FCSTD DOCUMENT  (FreeCAD 1.0R39319 (Git))
Label: Assignment_11.1_Knuckle_Joint_Assembly
License: All rights reserved
LicenseURL: https://en.wikipedia.org/wiki/All_rights_reserved
objects: TechDraw::DrawViewBalloon×10, App::FeaturePython×8, TechDraw::DrawViewAnnotation×6, TechDraw::DrawProjGroupItem×6, App::Link×5, TechDraw::DrawViewDimension×5, TechDraw::DrawSVGTemplate×2, TechDraw::DrawProjGroup×2, TechDraw::DrawPage×2, Assembly::JointGroup×1, Assembly::BomObject×1, Assembly::BomGroup×1, Spreadsheet::Sheet×1, TechDraw::DrawViewSpreadsheet×1, Assembly::ViewGroup×1, Assembly::AssemblyObject×1
note: 9 computed .brp shape members not serialized (recipe doc carries the construction recipe); baked Part::Feature solids carry a one-line shape summary decoded from their .brp
EXTERNAL_REF file=knuckle pin.FCStd obj=Body
EXTERNAL_REF file=Doube_eye.FCStd obj=Body
EXTERNAL_REF file=Eye End.FCStd obj=Body
EXTERNAL_REF file=taper pin.FCStd obj=Body
EXTERNAL_REF file=Coller.FCStd obj=Body

FEATURE [App::Link] knuckle_pin  label="knuckle pin"
  LinkedObject = -> <external knuckle pin.FCStd>#Body
FEATURE [App::FeaturePython] GroundedJoint  # Assembly grounded joint (typed FeaturePython)
  ObjectToGround = -> knuckle_pin
FEATURE [App::Link] Double_eye
  LinkPlacement = pos=(0,0,14.98) rot=(0,0,-1;1.56968rad)
  LinkedObject = -> <external Doube_eye.FCStd>#Body
  Placement = pos=(0,0,14.98) rot=(0,0,-1;1.56968rad)
FEATURE [App::Link] Single_Eye  label="Single Eye"
  LinkPlacement = pos=(0,0,37.0605) rot=(0,0,1;1.57134rad)
  LinkedObject = -> <external Eye End.FCStd>#Body
  Placement = pos=(0,0,37.0605) rot=(0,0,1;1.57134rad)
FEATURE [App::Link] taper_pin  label="taper pin"
  LinkPlacement = pos=(0,-27,102.1) rot=(1,0,0;4.71239rad)
  LinkedObject = -> <external taper pin.FCStd>#Body
  Placement = pos=(0,-27,102.1) rot=(1,0,0;4.71239rad)
FEATURE [App::FeaturePython] Joint  label="Revolute"  # Assembly joint (typed FeaturePython)
  Activated = true
  AngleMax = 130
  AngleMin = -15
  Detach1 = false
  Detach2 = false
  Distance = 0
  Distance2 = 0
  EnableAngleMax = true
  EnableAngleMin = true
  EnableLengthMax = false
  EnableLengthMin = false
  JointType = 1 (Revolute)
  LengthMax = 0
  LengthMin = 0
  Placement2 = pos=(0,0,14.98) rot=(0,0,1;0rad)
  Reference1 = -> Assembly [Double_eye.Face28,Double_eye.Edge1]
  Reference2 = -> Assembly [knuckle_pin.Face4,knuckle_pin.Edge1]
FEATURE [App::FeaturePython] Joint003  label="Fixed001"  # Assembly joint (typed FeaturePython)
  Activated = true
  AngleMax = 0
  AngleMin = 0
  Detach1 = false
  Detach2 = false
  Distance = 0
  Distance2 = 0
  EnableAngleMax = false
  EnableAngleMin = false
  EnableLengthMax = false
  EnableLengthMin = false
  JointType = 0 (Fixed)
  LengthMax = 0
  LengthMin = 0
  Offset2 = pos=(0,0,-25) rot=(0,0,1;0rad)
  Placement1 = pos=(0,1.42e-14,52) rot=(0,0,1;0rad)
  Placement2 = pos=(0,25,102.1) rot=(1,0,0;1.5708rad)
  Reference1 = -> Assembly [taper_pin.Face1,taper_pin.Edge3]
  Reference2 = -> Assembly [knuckle_pin.Face6,knuckle_pin.Face6]
FEATURE [App::FeaturePython] Joint004  label="Revolute001"  # Assembly joint (typed FeaturePython)
  Activated = true
  AngleMax = -70
  AngleMin = -180
  Detach1 = false
  Detach2 = false
  Distance = 0
  Distance2 = 0
  EnableAngleMax = true
  EnableAngleMin = true
  EnableLengthMax = false
  EnableLengthMin = false
  JointType = 1 (Revolute)
  LengthMax = 0
  LengthMin = 0
  Offset2 = pos=(0,0,7.215) rot=(0,0,1;0rad)
  Placement1 = pos=(0,0,35.98) rot=(0,0,1;0rad)
  Placement2 = pos=(0,0,73.0405) rot=(0,0,1;0rad)
  Reference1 = -> Assembly [Single_Eye.Edge41,Single_Eye.Edge41]
  Reference2 = -> Assembly [knuckle_pin.Face4,knuckle_pin.Face4]
FEATURE [TechDraw::DrawSVGTemplate] Template
  Height = 210
  Orientation = 1
  Template = C:/Program Files/FreeCAD 1.0/data/Mod/TechDraw/Templates/A4_Landscape_TD.svg
  Width = 297
FEATURE [TechDraw::DrawViewAnnotation] Annotation
  Font = osifont
  LineSpace = 100
  LockPosition = false
  MaxWidth = -1
  Rotation = 0
  ScaleType = 0
  Text = Front View
  TextSize = 5
  TextStyle = 0
  X = 108.227
  Y = 143.292
FEATURE [TechDraw::DrawViewAnnotation] Annotation001
  Font = osifont
  LineSpace = 100
  LockPosition = false
  MaxWidth = -1
  Rotation = 0
  ScaleType = 0
  Text = Top View
  TextSize = 5
  TextStyle = 0
  X = 108.227
  Y = 84.9012
FEATURE [TechDraw::DrawViewAnnotation] Annotation002
  Font = osifont
  LineSpace = 100
  LockPosition = false
  MaxWidth = -1
  Rotation = 0
  ScaleType = 0
  Text = Isometric View
  TextSize = 5
  TextStyle = 0
  X = 50.4437
  Y = 16.9549
FEATURE [TechDraw::DrawViewAnnotation] Annotation003
  Font = osifont
  LineSpace = 100
  LockPosition = false
  MaxWidth = -1
  Rotation = 0
  ScaleType = 0
  Text = Side View
  TextSize = 5
  TextStyle = 0
  X = 204.227
  Y = 143.292
FEATURE [App::Link] Coller
  LinkPlacement = pos=(0,0,95.1) rot=(0,0,1;1.5708rad)
  LinkedObject = -> <external Coller.FCStd>#Body
  Placement = pos=(0,0,95.1) rot=(0,0,1;1.5708rad)
FEATURE [App::FeaturePython] Joint005  label="Fixed"  # Assembly joint (typed FeaturePython)
  Activated = true
  AngleMax = 0
  AngleMin = 0
  Detach1 = false
  Detach2 = false
  Distance = 0
  Distance2 = 0
  EnableAngleMax = false
  EnableAngleMin = false
  EnableLengthMax = false
  EnableLengthMin = false
  JointType = 0 (Fixed)
  LengthMax = 0
  LengthMin = 0
  Offset2 = pos=(0,0,0) rot=(0,0,1;1.5708rad)
  Placement1 = pos=(0,0,7) rot=(0,0,1;0rad)
  Placement2 = pos=(0,0,102.1) rot=(0,0,1;1.5708rad)
  Reference1 = -> Assembly [Coller.Face6,Coller.Edge7]
  Reference2 = -> Assembly [knuckle_pin.Face4,knuckle_pin.Edge5]
FEATURE [Assembly::JointGroup] Joints
  Group = -> [GroundedJoint,Joint,Joint003,Joint004,Joint005]
FEATURE [Assembly::BomObject] Bill_of_Materials
  cells = A1='Index; B1='Name; C1='Quantity; A2='1; B2='knuckle pin; C2=1; A3='2; B3='Double_eye; C3=1; A4='3; B4='Single Eye; C4=1; A5='4; B5='taper pin; C5=1; A6='5; B6='Coller; C6=1
  columnsNames = Index | Name | Quantity
  detailParts = true
  detailSubAssemblies = true
  onlyParts = false
FEATURE [Assembly::BomGroup] Bills_of_Materials
  Group = -> [Bill_of_Materials]
FEATURE [Spreadsheet::Sheet] Spreadsheet
  cells = A1='Index; B1='Name; C1='Quantity; A2='1; B2='knuckle pin; C2=1; A3='2; B3='Double_eye; C3=1; A4='3; B4='Single Eye; C4=1; A5='4; B5='taper pin; C5=1; A6='5; B6='Coller; C6=1
FEATURE [TechDraw::DrawViewSpreadsheet] Sheet
  CellEnd = C6
  CellStart = A1
  Font = osifont
  LineWidth = 1.35
  LockPosition = false
  Rotation = 0
  ScaleType = 2
  Source = -> Bill_of_Materials
  Symbol = <blob: 3907 chars omitted>
  TextSize = 14
  X = 236.512
  Y = 91.6442
FEATURE [TechDraw::DrawViewAnnotation] Annotation004
  Font = osifont
  LineSpace = 100
  LockPosition = false
  MaxWidth = -1
  Rotation = 0
  ScaleType = 0
  Text = Bill of Material 
  TextSize = 4
  TextStyle = 0
  X = 236.512
  Y = 63.0244
FEATURE [TechDraw::DrawSVGTemplate] Template001
  Height = 210
  Orientation = 1
  Template = C:/Program Files/FreeCAD 1.0/data/Mod/TechDraw/Templates/A4_Landscape_TD.svg
  Width = 297
FEATURE [App::FeaturePython] Move  # WARN: FeaturePython — macro-defined, semantics opaque (R4)
  MoveType = 1
  MovementTransform = pos=(0,-2e-05,166) rot=(0,0,1;0rad)
  References = -> Assembly [knuckle_pin.,Double_eye.,Single_Eye.,taper_pin.,Coller.]
FEATURE [App::FeaturePython] Move001  # WARN: FeaturePython — macro-defined, semantics opaque (R4)
  MoveType = 0
  MovementTransform = pos=(73.0001,-3e-05,4e-05) rot=(-1.00436,0,0;0rad)
  References = -> Assembly [taper_pin.]
FEATURE [App::FeaturePython] Exploded_View  # WARN: FeaturePython — macro-defined, semantics opaque (R4)
  Group = -> [Move,Move001]
FEATURE [Assembly::ViewGroup] Exploded_Views
  Group = -> [Exploded_View]
FEATURE [Assembly::AssemblyObject] Assembly
  Group = -> [Joints,knuckle_pin,GroundedJoint,Double_eye,Single_Eye,taper_pin,Joint,Joint003,Joint004,Coller,Exploded_Views,Joint005,Bills_of_Materials,Exploded_View,Bill_of_Materials,Move,Move001]
  Origin = -> Origin
  Type = Assembly
FEATURE [TechDraw::DrawProjGroupItem] View  label="Front"
  CoarseView = false
  Direction = (0,-1,0)
  Focus = 100
  HardHidden = false
  IsoCount = 0
  IsoHidden = false
  IsoVisible = false
  LockPosition = true
  Perspective = false
  Rotation = 0
  RotationVector = (1,0,0)
  Scale = 0.25
  ScaleType = 2
  ScrubCount = 1
  SeamHidden = false
  SeamVisible = false
  SmoothHidden = false
  SmoothVisible = true
  Source = -> [Assembly]
  Type = 0
  X = 0
  XDirection = (1,0,0)
  Y = 0
FEATURE [TechDraw::DrawProjGroupItem] ProjItem  label="Top"
  CoarseView = false
  Direction = (0,0,1)
  Focus = 100
  HardHidden = false
  IsoCount = 0
  IsoHidden = false
  IsoVisible = false
  LockPosition = true
  Perspective = false
  Rotation = 0
  RotationVector = (1,0,0)
  Scale = 0.25
  ScaleType = 2
  ScrubCount = 1
  SeamHidden = false
  SeamVisible = false
  SmoothHidden = false
  SmoothVisible = true
  Source = -> [Assembly]
  Type = 4
  X = 0
  XDirection = (1,0,0)
  Y = -68.4206
FEATURE [TechDraw::DrawProjGroupItem] ProjItem001  label="Left"
  CoarseView = false
  Direction = (-1,-1e-16,0)
  Focus = 100
  HardHidden = false
  IsoCount = 0
  IsoHidden = false
  IsoVisible = false
  LockPosition = true
  Perspective = false
  Rotation = 0
  RotationVector = (1,0,0)
  Scale = 0.25
  ScaleType = 2
  ScrubCount = 1
  SeamHidden = false
  SeamVisible = false
  SmoothHidden = false
  SmoothVisible = true
  Source = -> [Assembly]
  Type = 1
  X = 96.1426
  XDirection = (1e-16,-1,0)
  Y = 0
FEATURE [TechDraw::DrawProjGroupItem] ProjItem002  label="FrontTopRight"
  CoarseView = false
  Direction = (0.57735,-0.57735,0.57735)
  Focus = 100
  HardHidden = false
  IsoCount = 0
  IsoHidden = false
  IsoVisible = false
  LockPosition = true
  Perspective = false
  Rotation = 0
  RotationVector = (1,0,0)
  Scale = 0.25
  ScaleType = 2
  ScrubCount = 1
  SeamHidden = false
  SeamVisible = false
  SmoothHidden = false
  SmoothVisible = true
  Source = -> [Assembly]
  Type = 7
  X = -57.6411
  XDirection = (0.707107,0.707107,0)
  Y = -123.101
FEATURE [TechDraw::DrawProjGroup] ProjGroup
  Anchor = -> View
  AutoDistribute = true
  LockPosition = false
  ProjectionType = 0
  Rotation = 0
  Scale = 0.25
  ScaleType = 1
  Source = -> [Assembly]
  Views = -> [View,ProjItem,ProjItem001,ProjItem002]
  X = 108.227
  Y = 167.894
  spacingX = 15
  spacingY = 15
FEATURE [TechDraw::DrawViewDimension] Dimension001
  AngleOverride = false
  Arbitrary = false
  ArbitraryTolerances = false
  BoxCorners = (2) [(-7.5,-14.625,-1e-07),(7.5,14.625,1e-07)]
  EqualTolerance = true
  ExtensionAngle = 0
  FormatSpec = %.2w
  FormatSpecOverTolerance = %+.2w
  FormatSpecUnderTolerance = %+.2w
  Inverted = false
  LineAngle = 0
  LockPosition = false
  MeasureType = 1
  OverTolerance = 0
  References2D = -> [ProjItem001]
  Rotation = 0
  ScaleType = 0
  TheoreticalExact = false
  Type = 0
  UnderTolerance = 0
  X = 27.0573
  Y = 0
FEATURE [TechDraw::DrawViewDimension] Dimension
  AngleOverride = false
  Arbitrary = false
  ArbitraryTolerances = false
  BoxCorners = (2) [(-43.3781,-14.625,-1e-07),(43.3781,14.625,1e-07)]
  EqualTolerance = true
  ExtensionAngle = 0
  FormatSpec = %.2w
  FormatSpecOverTolerance = %+.2w
  FormatSpecUnderTolerance = %+.2w
  Inverted = false
  LineAngle = 0
  LockPosition = false
  MeasureType = 1
  OverTolerance = 0
  References2D = -> [View]
  Rotation = 0
  ScaleType = 0
  TheoreticalExact = false
  Type = 0
  UnderTolerance = 0
  X = -0.000147
  Y = 32.917
FEATURE [TechDraw::DrawViewBalloon] Balloon
  BubbleShape = 0
  EndType = 0
  EndTypeScale = 1
  KinkLength = 5
  LockPosition = false
  OriginX = 3.36178
  OriginY = -57.0902
  Rotation = 0
  ScaleType = 0
  ShapeScale = 0.8
  SourceView = -> View
  Text = 1
  TextWrapLen = -1
  X = 94.7676
  Y = -79.7421
FEATURE [TechDraw::DrawViewBalloon] Balloon001
  BubbleShape = 0
  EndType = 0
  EndTypeScale = 1
  KinkLength = 5
  LockPosition = false
  OriginX = 51.8363
  OriginY = 24.6512
  Rotation = 0
  ScaleType = 0
  ShapeScale = 0.8
  SourceView = -> View
  Text = 2
  TextWrapLen = -1
  X = 129.46
  Y = 53.5628
FEATURE [TechDraw::DrawViewBalloon] Balloon002
  BubbleShape = 0
  EndType = 0
  EndTypeScale = 0.9
  KinkLength = 5
  LockPosition = false
  OriginX = -126.379
  OriginY = 17.9415
  Rotation = 0
  ScaleType = 0
  ShapeScale = 0.8
  SourceView = -> ProjItem
  Text = 3
  TextWrapLen = -1
  X = -138.193
  Y = 87.6891
FEATURE [TechDraw::DrawViewBalloon] Balloon003
  BubbleShape = 0
  EndType = 0
  EndTypeScale = 1
  KinkLength = 5
  LockPosition = false
  OriginX = 26.6327
  OriginY = 48.4784
  Rotation = 0
  ScaleType = 0
  ShapeScale = 0.8
  SourceView = -> ProjItem001
  Text = 4
  TextWrapLen = -1
  X = 82.7868
  Y = 94.8136
FEATURE [TechDraw::DrawViewBalloon] Balloon004
  BubbleShape = 0
  EndType = 0
  EndTypeScale = 1
  KinkLength = 5
  LockPosition = false
  OriginX = -3.66518
  OriginY = 9.87877
  Rotation = 0
  ScaleType = 0
  ShapeScale = 0.8
  SourceView = -> Balloon003
  Text = 5
  TextWrapLen = -1
  X = -24.8614
  Y = -3.60584
FEATURE [TechDraw::DrawProjGroupItem] View001  label="Front001"
  CoarseView = false
  Direction = (0,-1,0)
  Focus = 100
  HardHidden = false
  IsoCount = 0
  IsoHidden = false
  IsoVisible = false
  LockPosition = true
  Perspective = false
  Rotation = 0
  RotationVector = (1,0,0)
  Scale = 0.5
  ScaleType = 2
  ScrubCount = 1
  SeamHidden = false
  SeamVisible = false
  SmoothHidden = false
  SmoothVisible = true
  Source = -> [Exploded_View]
  Type = 0
  X = 0
  XDirection = (1,0,0)
  Y = 0
FEATURE [TechDraw::DrawViewAnnotation] Annotation005
  Font = osifont
  LineSpace = 100
  LockPosition = false
  MaxWidth = -1
  Rotation = 0
  ScaleType = 0
  Text = Exploded View
  TextSize = 5
  TextStyle = 0
  X = 143.116
  Y = 68.226
FEATURE [TechDraw::DrawProjGroupItem] ProjItem003  label="FrontTopLeft"
  CoarseView = false
  Direction = (-0.57735,-0.57735,0.57735)
  Focus = 100
  HardHidden = false
  IsoCount = 0
  IsoHidden = false
  IsoVisible = false
  LockPosition = true
  Perspective = false
  Rotation = 0
  RotationVector = (1,0,0)
  Scale = 0.5
  ScaleType = 2
  ScrubCount = 1
  SeamHidden = false
  SeamVisible = false
  SmoothHidden = false
  SmoothVisible = true
  Source = -> [Exploded_View]
  Type = 6
  X = -5.38404
  XDirection = (0.707107,-0.707107,0)
  Y = 13.7785
FEATURE [TechDraw::DrawProjGroup] ProjGroup001
  Anchor = -> View001
  AutoDistribute = true
  LockPosition = false
  ProjectionType = 0
  Rotation = 0
  Scale = 0.5
  ScaleType = 2
  Source = -> [Exploded_View]
  Views = -> [View001,ProjItem003]
  X = 148.5
  Y = 105
  spacingX = 15
  spacingY = 15
FEATURE [TechDraw::DrawViewBalloon] Balloon005
  BubbleShape = 0
  EndType = 0
  EndTypeScale = 1
  KinkLength = 5
  LockPosition = false
  OriginX = -33.0978
  OriginY = 24.9603
  Rotation = 0
  ScaleType = 0
  ShapeScale = 1
  SourceView = -> ProjItem003
  Text = 1
  TextWrapLen = -1
  X = -86.6454
  Y = 54.4689
FEATURE [TechDraw::DrawViewBalloon] Balloon006
  BubbleShape = 0
  EndType = 0
  EndTypeScale = 1
  KinkLength = 5
  LockPosition = false
  OriginX = 105.038
  OriginY = 3.10335
  Rotation = 0
  ScaleType = 0
  ShapeScale = 1
  SourceView = -> ProjItem003
  Text = 2
  TextWrapLen = -1
  X = 160.775
  Y = 16.0008
FEATURE [TechDraw::DrawViewBalloon] Balloon007
  BubbleShape = 0
  EndType = 0
  EndTypeScale = 1
  KinkLength = 5
  LockPosition = false
  OriginX = -128.394
  OriginY = -38.8619
  Rotation = 0
  ScaleType = 0
  ShapeScale = 1
  SourceView = -> ProjItem003
  Text = 3
  TextWrapLen = -1
  X = -171.45
  Y = 5.50947
FEATURE [TechDraw::DrawViewBalloon] Balloon008
  BubbleShape = 0
  EndType = 0
  EndTypeScale = 1
  KinkLength = 5
  LockPosition = false
  OriginX = 51.707
  OriginY = 118.508
  Rotation = 0
  ScaleType = 0
  ShapeScale = 1
  SourceView = -> ProjItem003
  Text = 4
  TextWrapLen = -1
  X = 91.707
  Y = 132.28
FEATURE [TechDraw::DrawViewBalloon] Balloon009
  BubbleShape = 0
  EndType = 0
  EndTypeScale = 1
  KinkLength = 5
  LockPosition = false
  OriginX = -39.2177
  OriginY = 96.6509
  Rotation = 0
  ScaleType = 0
  ShapeScale = 1
  SourceView = -> ProjItem003
  Text = 5
  TextWrapLen = -1
  X = -88.3939
  Y = 106.051
FEATURE [TechDraw::DrawPage] Page001
  KeepUpdated = true
  NextBalloonIndex = 7
  ProjectionType = 0
  Template = -> Template001
  Views = -> [ProjGroup001,Annotation005,Balloon005,Balloon006,Balloon007,Balloon008,Balloon009]
FEATURE [TechDraw::DrawViewDimension] Dimension002
  AngleOverride = false
  Arbitrary = false
  ArbitraryTolerances = false
  BoxCorners = (2) [(-43.3781,-7.5,-1e-07),(43.3781,7.5,1e-07)]
  EqualTolerance = true
  ExtensionAngle = 0
  FormatSpec = %.2w
  FormatSpecOverTolerance = %+.2w
  FormatSpecUnderTolerance = %+.2w
  Inverted = false
  LineAngle = 0
  LockPosition = false
  MeasureType = 1
  OverTolerance = 0
  References2D = -> [ProjItem]
  Rotation = 0
  ScaleType = 0
  TheoreticalExact = false
  Type = 0
  UnderTolerance = 0
  X = -49.002
  Y = 16.2062
FEATURE [TechDraw::DrawViewDimension] Dimension003
  AngleOverride = false
  Arbitrary = false
  ArbitraryTolerances = false
  BoxCorners = (2) [(-43.3781,-7.5,-1e-07),(43.3781,7.5,1e-07)]
  EqualTolerance = true
  ExtensionAngle = 0
  FormatSpec = R%.2w
  FormatSpecOverTolerance = %+.2w
  FormatSpecUnderTolerance = %+.2w
  Inverted = false
  LineAngle = 0
  LockPosition = false
  MeasureType = 1
  OverTolerance = 0
  References2D = -> [ProjItem]
  Rotation = 0
  ScaleType = 0
  TheoreticalExact = false
  Type = 4
  UnderTolerance = 0
  X = -8.61617
  Y = 25.7406
FEATURE [TechDraw::DrawViewDimension] Dimension004
  AngleOverride = false
  Arbitrary = false
  ArbitraryTolerances = false
  BoxCorners = (2) [(-43.3781,-7.5,-1e-07),(43.3781,7.5,1e-07)]
  EqualTolerance = true
  ExtensionAngle = 0
  FormatSpec = %.2w
  FormatSpecOverTolerance = %+.2w
  FormatSpecUnderTolerance = %+.2w
  Inverted = false
  LineAngle = 0
  LockPosition = false
  MeasureType = 1
  OverTolerance = 0
  References2D = -> [ProjItem]
  Rotation = 0
  ScaleType = 0
  TheoreticalExact = false
  Type = 0
  UnderTolerance = 0
  X = 62.2616
  Y = 14.8713
FEATURE [TechDraw::DrawPage] Page
  KeepUpdated = true
  NextBalloonIndex = 6
  ProjectionType = 0
  Template = -> Template
  Views = -> [ProjGroup,Dimension001,Annotation,Annotation001,Annotation002,Annotation003,Dimension,Sheet,Annotation004,Balloon,Balloon001,Balloon002,Balloon003,Balloon004,Dimension002,Dimension003,Dimension004]

RESOLVED EXTERNAL PARTS (link-assembly join: the EXTERNAL_REF files above that resolve inside this repo's crawl, each included once):
---- part Coller.FCStd = doc fcstd_88898c6e48c1 ----
FCSTD DOCUMENT  (FreeCAD 1.0R39319 (Git))
Label: Coller
License: All rights reserved
LicenseURL: https://en.wikipedia.org/wiki/All_rights_reserved
objects: Sketcher::SketchObject×2, PartDesign::Pad×1, PartDesign::Pocket×1, PartDesign::Body×1
note: 11 computed .brp shape members not serialized (recipe doc carries the construction recipe); baked Part::Feature solids carry a one-line shape summary decoded from their .brp

FEATURE [Sketcher::SketchObject] Sketch
  ArcFitTolerance = 1e-06
  AttachmentSupport = -> [XY_Plane]
  FullyConstrained = true
  MakeInternals = false
  MapMode = 5
  sketch-geometry (2):
    g0: Circle CenterX=0 CenterY=0 CenterZ=0 NormalX=0 NormalY=0 NormalZ=1 AngleXU=0 Radius=22.5
    g1: Circle CenterX=0 CenterY=0 CenterZ=0 NormalX=0 NormalY=0 NormalZ=1 AngleXU=0 Radius=15
  constraints (4):
    c: Coincident(g0,g-1)
    c: Coincident(g1,g0)
    c: Diameter(g0) = 45
    c: Diameter(g1) = 30
FEATURE [PartDesign::Pad] Pad
  Direction = (0,0,1)
  Length = 14
  Length2 = 10
  Profile = -> Sketch
  ReferenceAxis = -> Sketch [N_Axis]
  Refine = true
  Suppressed = false
  Type = 0
FEATURE [Sketcher::SketchObject] Sketch001
  ArcFitTolerance = 1e-06
  AttachmentOffset = pos=(0,7,22.5) rot=(0,0,1;0rad)
  AttachmentSupport = -> [YZ_Plane]
  FullyConstrained = true
  MakeInternals = false
  MapMode = 5
  Placement = pos=(22.5,0,7) rot=(0.57735,0.57735,0.57735;2.0944rad)
  sketch-geometry (1):
    g0: Circle CenterX=0 CenterY=0 CenterZ=0 NormalX=0 NormalY=0 NormalZ=1 AngleXU=0 Radius=3
  constraints (2):
    c: Coincident(g0,g-1)
    c: Diameter(g0) = 6
FEATURE [PartDesign::Pocket] Pocket
  BaseFeature = -> Pad
  Direction = (-1,0,0)
  Length = 5
  Length2 = 5
  Profile = -> Sketch001
  ReferenceAxis = -> Sketch001 [N_Axis]
  Refine = true
  Suppressed = false
  Type = 1
FEATURE [PartDesign::Body] Body  label="Coller"
  AllowCompound = false
  Group = -> [Sketch,Pad,Sketch001,Pocket]
  Origin = -> Origin
  Tip = -> Pocket
---- part Doube_eye.FCStd = doc fcstd_e9481a9b5fc3 ----
FCSTD DOCUMENT  (FreeCAD 1.0R39319 (Git))
Label: Doube_eye
License: All rights reserved
LicenseURL: https://en.wikipedia.org/wiki/All_rights_reserved
objects: Sketcher::SketchObject×4, PartDesign::Pad×2, PartDesign::Pocket×2, PartDesign::Fillet×2, PartDesign::Body×1
note: 27 computed .brp shape members not serialized (recipe doc carries the construction recipe); baked Part::Feature solids carry a one-line shape summary decoded from their .brp

FEATURE [Sketcher::SketchObject] Sketch
  ArcFitTolerance = 1e-06
  AttachmentSupport = -> [XY_Plane]
  FullyConstrained = true
  MakeInternals = false
  MapMode = 5
  sketch-geometry (6):
    g0: ArcOfCircle CenterX=0 CenterY=0 CenterZ=0 NormalX=0 NormalY=0 NormalZ=1 AngleXU=0 Radius=30 StartAngle=2.2143 EndAngle=7.21048
    g1: Circle CenterX=0 CenterY=0 CenterZ=0 NormalX=0 NormalY=0 NormalZ=1 AngleXU=0 Radius=15
    g2: LineSegment StartX=18 StartY=24 StartZ=0 EndX=18 EndY=147 EndZ=0
    g3: LineSegment StartX=18 StartY=147 StartZ=0 EndX=-18 EndY=147 EndZ=0
    g4: LineSegment StartX=-18 StartY=147 StartZ=0 EndX=-18 EndY=24 EndZ=0
    g5: GeomPoint [constr] X=0 Y=85.5 Z=0
  constraints (15):
    c: Coincident(g0,g-1)
    c: Diameter(g0) = 60
    c: Coincident(g1,g0)
    c: Diameter(g1) = 30
    c: Coincident(g2,g3)
    c: Coincident(g3,g4)
    c: Vertical(g2)
    c: Vertical(g4)
    c: Horizontal(g3)
    c: Symmetric(g4,g2,g5)
    c: PointOnObject(g5,g-2)
    c: Distance(g3,g3) = 36
    c: Coincident(g0,g2)
    c: Coincident(g0,g4)
    c: Distance(g0,g3) = 147
FEATURE [PartDesign::Pad] Pad
  Direction = (0,0,1)
  Length = 80
  Length2 = 10
  Profile = -> Sketch
  ReferenceAxis = -> Sketch [N_Axis]
  Refine = true
  Suppressed = false
  Type = 0
FEATURE [Sketcher::SketchObject] Sketch001
  ArcFitTolerance = 1e-06
  AttachmentOffset = pos=(0,40,15) rot=(0,0,1;0rad)
  AttachmentSupport = -> [Pad]
  ExternalGeometry = -> [Pad]
  FullyConstrained = true
  MakeInternals = false
  MapMode = 5
  Placement = pos=(33,0,40) rot=(0.57735,0.57735,0.57735;2.0944rad)
  sketch-geometry (12):
    g0: LineSegment StartX=-34 StartY=-18 StartZ=0 EndX=36 EndY=-18 EndZ=0
    g1: LineSegment StartX=36 StartY=18 StartZ=0 EndX=-34 EndY=18 EndZ=0
    g2: LineSegment StartX=-34 StartY=18 StartZ=0 EndX=-34 EndY=-18 EndZ=0
    g3: ArcOfCircle CenterX=36 CenterY=2.6e-15 CenterZ=0 NormalX=0 NormalY=0 NormalZ=1 AngleXU=0 Radius=18 StartAngle=4.71239 EndAngle=7.85398
    g4: ArcOfCircle CenterX=36 CenterY=2.6e-15 CenterZ=0 NormalX=0 NormalY=0 NormalZ=1 AngleXU=0 Radius=40 StartAngle=4.71239 EndAngle=5.81642
    g5: LineSegment StartX=147 StartY=18 StartZ=0 EndX=71.7211 EndY=18 EndZ=0
    g6: ArcOfCircle CenterX=36 CenterY=2.6e-15 CenterZ=0 NormalX=0 NormalY=0 NormalZ=1 AngleXU=0 Radius=40 StartAngle=0.466765 EndAngle=1.5708
    g7: LineSegment StartX=147 StartY=-18 StartZ=0 EndX=147 EndY=-40 EndZ=0
    g8: LineSegment StartX=147 StartY=-40 StartZ=0 EndX=36 EndY=-40 EndZ=0
    g9: LineSegment StartX=147 StartY=18 StartZ=0 EndX=147 EndY=40 EndZ=0
    g10: LineSegment StartX=147 StartY=40 StartZ=0 EndX=36 EndY=40 EndZ=0
    g11: LineSegment StartX=147 StartY=-18 StartZ=0 EndX=71.7211 EndY=-18 EndZ=0
  constraints (31):
    c: Coincident(g1,g2)
    c: Coincident(g2,g0)
    c: Horizontal(g0)
    c: Horizontal(g1)
    c: Vertical(g2)
    c: DistanceY(g2,g2) = 36
    c: Coincident(g4,g3)
    c: Tangent(g1,g3) = -1.5708
    c: Distance(g3,g-1) = 36
    c: Distance(g3,g2) = 70
    c: Horizontal(g5)
    c: Distance(g7,g5) = 36
    c: Equal(g4,g6)
    c: Coincident(g4,g6)
    c: Vertical(g6,g3)
    c: Coincident(g6,g5)
    c: Tangent(g4,g-4) = 1.5708
    c: Vertical(g7)
    c: Coincident(g7,g8)
    c: Coincident(g8,g4)
    c: Coincident(g5,g9)
    c: Coincident(g9,g10)
    c: Coincident(g10,g6)
    c: Coincident(g7,g11)
    c: Coincident(g11,g4)
    c: Horizontal(g11)
    c: Coincident(g9,g-8)
    c: Symmetric(g5,g7,g-1)
    c: Coincident(g7,g-8)
    c: PointOnObject(g6,g-3)
    c: Tangent(g3,g0) = -1.5708
FEATURE [PartDesign::Pocket] Pocket
  BaseFeature = -> Pad
  Direction = (-1,0,0)
  Length = 5
  Length2 = 5
  Profile = -> Sketch001
  ReferenceAxis = -> Sketch001 [N_Axis]
  Refine = true
  Suppressed = false
  Type = 1
FEATURE [PartDesign::Fillet] Fillet
  Base = -> Pocket [Edge35,Edge31]
  BaseFeature = -> Pocket
  Radius = 10
  Refine = true
  SupportTransform = false
  Suppressed = false
  UseAllEdges = false
FEATURE [Sketcher::SketchObject] Sketch002
  ArcFitTolerance = 1e-06
  AttachmentSupport = -> [Fillet]
  ExternalGeometry = -> [Fillet]
  FullyConstrained = true
  MakeInternals = false
  MapMode = 5
  Placement = pos=(0,147,0) rot=(0,0.707107,0.707107;3.14159rad)
  sketch-geometry (12):
    g0: LineSegment StartX=-18 StartY=58 StartZ=0 EndX=-10.9289 EndY=58 EndZ=0
    g1: LineSegment StartX=-10.9289 StartY=58 StartZ=0 EndX=-18 EndY=50.9289 EndZ=0
    g2: LineSegment StartX=-18 StartY=50.9289 StartZ=0 EndX=-18 EndY=58 EndZ=0
    g3: LineSegment StartX=-18 StartY=22 StartZ=0 EndX=-10.9289 EndY=22 EndZ=0
    g4: LineSegment StartX=-10.9289 StartY=22 StartZ=0 EndX=-18 EndY=29.0711 EndZ=0
    g5: LineSegment StartX=-18 StartY=29.0711 StartZ=0 EndX=-18 EndY=22 EndZ=0
    g6: LineSegment StartX=18 StartY=22 StartZ=0 EndX=10.9289 EndY=22 EndZ=0
    g7: LineSegment StartX=10.9289 StartY=22 StartZ=0 EndX=18 EndY=29.0711 EndZ=0
    g8: LineSegment StartX=18 StartY=29.0711 StartZ=0 EndX=18 EndY=22 EndZ=0
    g9: LineSegment StartX=18 StartY=58 StartZ=0 EndX=10.9289 EndY=58 EndZ=0
    g10: LineSegment StartX=10.9289 StartY=58 StartZ=0 EndX=18 EndY=50.9289 EndZ=0
    g11: LineSegment StartX=18 StartY=50.9289 StartZ=0 EndX=18 EndY=58 EndZ=0
  constraints (32):
    c: Coincident(g-4,g0)
    c: PointOnObject(g0,g-3)
    c: Coincident(g0,g1)
    c: PointOnObject(g1,g-4)
    c: Coincident(g1,g2)
    c: Coincident(g-6,g3)
    c: PointOnObject(g3,g-6)
    c: Coincident(g3,g4)
    c: PointOnObject(g4,g-4)
    c: Coincident(g4,g5)
    c: Coincident(g5,g3)
    c: Coincident(g-6,g6)
    c: PointOnObject(g6,g-6)
    c: Coincident(g6,g7)
    c: PointOnObject(g7,g-5)
    c: Coincident(g7,g8)
    c: Coincident(g8,g6)
    c: Coincident(g-5,g9)
    c: PointOnObject(g9,g-3)
    c: Coincident(g9,g10)
    c: PointOnObject(g10,g-5)
    c: Coincident(g10,g11)
    c: Coincident(g11,g9)
    c: Equal(g2,g0)
    c: Equal(g9,g11)
    c: Equal(g8,g6)
    c: Equal(g3,g5)
    c: Distance(g1,g1) = 10
    c: Distance(g10,g10) = 10
    c: Distance(g7,g7) = 10
    c: Distance(g4,g4) = 10
    c: Coincident(g2,g0)
FEATURE [PartDesign::Pocket] Pocket001
  BaseFeature = -> Fillet
  Direction = (0,-1,2e-16)
  Length = 45
  Length2 = 5
  Profile = -> Sketch002
  ReferenceAxis = -> Sketch002 [N_Axis]
  Refine = true
  Suppressed = false
  Type = 0
FEATURE [PartDesign::Fillet] Fillet001
  Base = -> Pocket001 [Edge69,Edge28,Edge70,Edge36]
  BaseFeature = -> Pocket001
  Radius = 4
  Refine = true
  SupportTransform = false
  Suppressed = false
  UseAllEdges = false
FEATURE [Sketcher::SketchObject] Sketch003
  ArcFitTolerance = 1e-06
  AttachmentOffset = pos=(0,40,0) rot=(0,0,1;0rad)
  AttachmentSupport = -> [Fillet001]
  FullyConstrained = true
  MakeInternals = false
  MapMode = 5
  Placement = pos=(0,147,40) rot=(0,0.707107,0.707107;3.14159rad)
  sketch-geometry (1):
    g0: Circle CenterX=0 CenterY=0 CenterZ=0 NormalX=0 NormalY=0 NormalZ=1 AngleXU=0 Radius=15
  constraints (2):
    c: Coincident(g0,g-1)
    c: Diameter(g0) = 30
FEATURE [PartDesign::Pad] Pad001
  BaseFeature = -> Fillet001
  Direction = (0,1,-2e-16)
  Length = 40
  Length2 = 10
  Profile = -> Sketch003
  ReferenceAxis = -> Sketch003 [N_Axis]
  Refine = true
  Suppressed = false
  Type = 0
FEATURE [PartDesign::Body] Body  label="Double_eye"
  AllowCompound = false
  Group = -> [Sketch,Pad,Sketch001,Pocket,Fillet,Sketch002,Pocket001,Fillet001,Sketch003,Pad001]
  Origin = -> Origin
  Tip = -> Pad001
